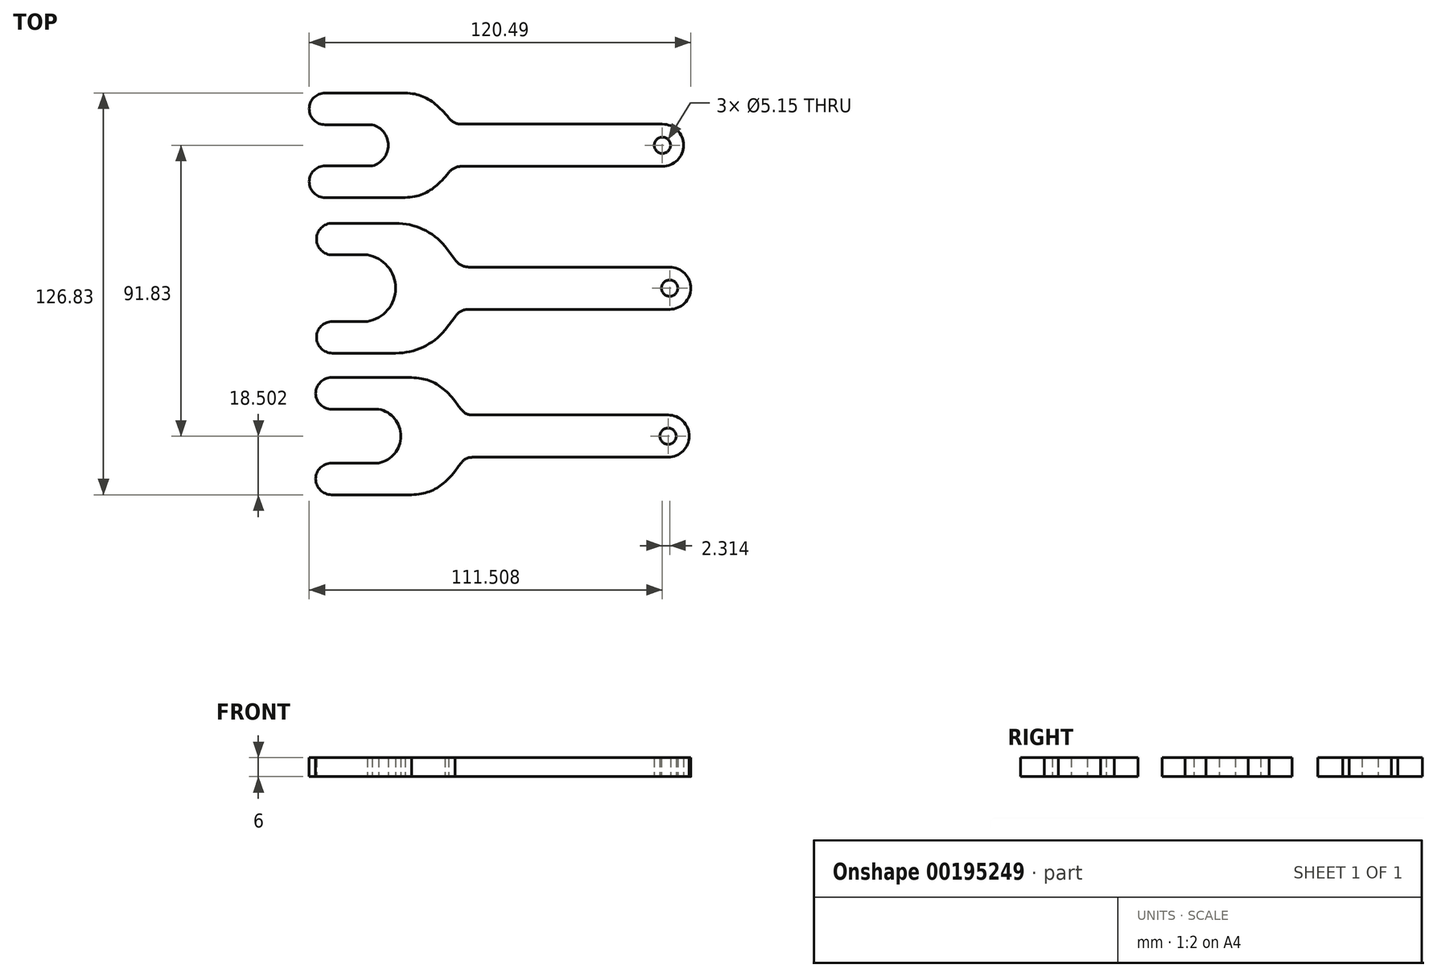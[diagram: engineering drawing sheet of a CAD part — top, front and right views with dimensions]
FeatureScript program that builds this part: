
annotation { "Feature Type Name" : "Feature", "Feature Type Description" : "" }
export const myFeature = defineFeature(function(context is Context, id is Id, definition is map)
    precondition{}
    {
        {
            var Q0;
            Q0=qCreatedBy(makeId("Top.planeOp"),FACE);
            var sketch = newSketch(context, id + "F0", { "sketchPlane" : qUnion([Q0])});
            skLineSegment(sketch, "E0.bottom", {"start": v(1.68, -10.5) * mm, "end": v(-4.7, -10.5) * mm});
            skLineSegment(sketch, "E0.top", {"start": v(1.68, 10.5) * mm, "end": v(-4.7, 10.5) * mm});
            skLineSegment(sketch, "E0.left", {"start": v(1.68, -10.5) * mm, "end": v(1.68, 10.5) * mm, "construction": true});
            skLineSegment(sketch, "E0.right", {"start": v(-4.7, -10.5) * mm, "end": v(-4.7, 10.5) * mm, "construction": true});
            skArc(sketch, "E1.trimOffspring", {"start": v(1.68, -10.5) * mm, "mid": v(10.63, 0) * mm, "end": v(1.68, 10.5) * mm});
            skPoint(sketch, "E2.oppositeSnap0", {"position": v(10.63, 0) * mm});
            skLineSegment(sketch, "E2.bottom", {"start": v(-9.33, -10.5) * mm, "end": v(1.68, -10.5) * mm});
            skLineSegment(sketch, "E2.top", {"start": v(-9.33, -20.5) * mm, "end": v(10.63, -20.5) * mm});
            skLineSegment(sketch, "E3.bottom", {"start": v(-4.7, 10.5) * mm, "end": v(-9.33, 10.5) * mm});
            skLineSegment(sketch, "E4.top", {"start": v(-4.7, 10.5) * mm, "end": v(1.68, 10.5) * mm});
            skLineSegment(sketch, "E5", {"start": v(10.63, 20.5) * mm, "end": v(-9.33, 20.5) * mm});
            skArc(sketch, "E6", {"start": v(10.63, -20.5) * mm, "mid": v(20.48, -17.98) * mm, "end": v(27.9, -11.05) * mm});
            skArc(sketch, "E7", {"start": v(-9.33, 20.5) * mm, "mid": v(-14.33, 15.5) * mm, "end": v(-9.33, 10.5) * mm});
            skArc(sketch, "E8", {"start": v(-9.33, -10.5) * mm, "mid": v(-14.33, -15.5) * mm, "end": v(-9.33, -20.5) * mm});
            skPoint(sketch, "E9.oppositeSnap0", {"position": v(31.13, 0) * mm});
            skLineSegment(sketch, "E10.top", {"start": v(33.66, 6.67) * mm, "end": v(97.17, 6.67) * mm});
            skLineSegment(sketch, "E11.MirrorCS", {"start": v(33.66, -6.67) * mm, "end": v(97.17, -6.67) * mm});
            skArc(sketch, "E12", {"start": v(97.17, 6.67) * mm, "mid": v(103.84, 0) * mm, "end": v(97.17, -6.67) * mm});
            skLineSegment(sketch, "E13", {"start": v(29.63, 8.7) * mm, "end": v(26.27, 13.25) * mm});
            skLineSegment(sketch, "E14", {"start": v(26.27, -13.25) * mm, "end": v(29.63, -8.7) * mm});
            skCircle(sketch, "E15", {"center": v(97.17, 0) * mm, "radius": 2.57 * mm});
            skPoint(sketch, "E16.MirrorCS.end.orphan", {"position": v(97.17, -6.67) * mm});
            skArc(sketch, "E17.trimOffspring", {"start": v(27.9, 11.05) * mm, "mid": v(20.48, 17.98) * mm, "end": v(10.63, 20.5) * mm});
            skPoint(sketch, "E18.MirrorCS.end.orphan", {"position": v(31.13, -6.67) * mm});
            skPoint(sketch, "E19.visualSharp", {"position": v(31.13, 6.67) * mm});
            skArc(sketch, "E19.filletArc", {"start": v(29.63, 8.7) * mm, "mid": v(31.4, 7.2) * mm, "end": v(33.66, 6.67) * mm});
            skArc(sketch, "E20.filletArc", {"start": v(33.66, -6.67) * mm, "mid": v(31.4, -7.2) * mm, "end": v(29.63, -8.7) * mm});
            skSolve(sketch);
        }
        {
            var Q0;
            {var subQ5=sQuery(id+"F0.wireOp",EDGE,"E1.trimOffspring");Q0=makeQuery(id+"F0.imprint","IMPRINT",FACE,{"disambiguationData":[TD([[makeQuery(id+"F0.imprint","IMPRINT",EDGE,{"derivedFrom":subQ5}),-1.0]])]});}
            extrude(context, id + "F1", {"entities" : qUnion([Q0]), "depth" : 6 * mm});
        }
        {
            var Q0;
            Q0=qCreatedBy(makeId("Top.planeOp"),FACE);
            var sketch = newSketch(context, id + "F2", { "sketchPlane" : qUnion([Q0])});
            skLineSegment(sketch, "E21.bottom", {"start": v(3.28, 38.62) * mm, "end": v(-3.08, 38.62) * mm});
            skLineSegment(sketch, "E21.top", {"start": v(3.28, 51.62) * mm, "end": v(-3.08, 51.62) * mm});
            skLineSegment(sketch, "E21.left", {"start": v(3.28, 38.62) * mm, "end": v(3.28, 51.62) * mm, "construction": true});
            skLineSegment(sketch, "E21.right", {"start": v(-3.08, 38.62) * mm, "end": v(-3.08, 51.62) * mm, "construction": true});
            skArc(sketch, "E22.trimOffspring", {"start": v(3.28, 38.62) * mm, "mid": v(8.32, 45.12) * mm, "end": v(3.28, 51.62) * mm});
            skPoint(sketch, "E23.oppositeSnap0", {"position": v(8.32, 45.12) * mm});
            skLineSegment(sketch, "E23.bottom", {"start": v(-11.65, 38.62) * mm, "end": v(3.28, 38.62) * mm});
            skLineSegment(sketch, "E24.bottom", {"start": v(-3.08, 51.62) * mm, "end": v(-11.65, 51.62) * mm});
            skLineSegment(sketch, "E25.top", {"start": v(-3.08, 51.62) * mm, "end": v(3.28, 51.62) * mm});
            skArc(sketch, "E26", {"start": v(-11.65, 61.62) * mm, "mid": v(-16.65, 56.62) * mm, "end": v(-11.65, 51.62) * mm});
            skPoint(sketch, "E27.oppositeSnap0", {"position": v(28.82, 45.12) * mm});
            skLineSegment(sketch, "E28.top", {"start": v(31.34, 51.8) * mm, "end": v(94.86, 51.8) * mm});
            skLineSegment(sketch, "E29.MirrorCS", {"start": v(31.34, 38.45) * mm, "end": v(94.86, 38.45) * mm});
            skArc(sketch, "E30", {"start": v(94.86, 51.8) * mm, "mid": v(101.53, 45.12) * mm, "end": v(94.86, 38.45) * mm});
            skCircle(sketch, "E31", {"center": v(94.86, 45.12) * mm, "radius": 2.57 * mm});
            skPoint(sketch, "E32.orphan", {"position": v(98.78, 49.12) * mm});
            skPoint(sketch, "E33.MirrorCS.end.orphan", {"position": v(98.78, 42.45) * mm});
            skPoint(sketch, "E34.MirrorCS.end.orphan", {"position": v(32.74, 42.45) * mm});
            skPoint(sketch, "E34.MirrorCS.start.orphan", {"position": v(32.74, 49.12) * mm});
            skPoint(sketch, "E35.visualSharp", {"position": v(28.82, 51.8) * mm});
            skArc(sketch, "E35.filletArc", {"start": v(27.32, 53.82) * mm, "mid": v(29.09, 52.33) * mm, "end": v(31.34, 51.8) * mm});
            skPoint(sketch, "E36.visualSharp", {"position": v(28.82, 38.45) * mm});
            skArc(sketch, "E36.filletArc", {"start": v(31.34, 38.45) * mm, "mid": v(29.09, 37.91) * mm, "end": v(27.32, 36.42) * mm});
            skLineSegment(sketch, "E37", {"start": v(-11.65, 61.62) * mm, "end": v(13.65, 61.62) * mm});
            skLineSegment(sketch, "E38", {"start": v(-11.65, 51.62) * mm, "end": v(-11.65, 61.62) * mm, "construction": true});
            skLineSegment(sketch, "E39", {"start": v(112.27, 45.12) * mm, "end": v(-30.7, 45.12) * mm, "construction": true});
            skLineSegment(sketch, "E40.MirrorCS", {"start": v(-11.65, 28.62) * mm, "end": v(13.65, 28.62) * mm});
            skArc(sketch, "E41.MirrorCS", {"start": v(-11.65, 28.62) * mm, "mid": v(-16.65, 33.62) * mm, "end": v(-11.65, 38.62) * mm});
            skFitSpline(sketch, "E42", {"points": [v(13.65, 61.62) * mm, v(27.32, 53.82) * mm], "startDerivative": vector(18.4, -0.56) * mm, "endDerivative": vector(11.88, -14.56) * mm});
            skFitSpline(sketch, "E43.MirrorCS", {"points": [v(13.65, 28.62) * mm, v(27.32, 36.42) * mm], "startDerivative": vector(18.4, 0.56) * mm, "endDerivative": vector(11.88, 14.56) * mm});
            skSolve(sketch);
        }
        {
            var Q0;
            {var subQ1=sQuery(id+"F2.wireOp",EDGE,"E22.trimOffspring");Q0=makeQuery(id+"F2.imprint","IMPRINT",FACE,{"disambiguationData":[TD([[makeQuery(id+"F2.imprint","IMPRINT",EDGE,{"derivedFrom":subQ1}),-1.0]])]});}
            extrude(context, id + "F3", {"entities" : qUnion([Q0]), "depth" : 6 * mm});
        }
        {
            var Q0;
            Q0=qCreatedBy(makeId("Top.planeOp"),FACE);
            var sketch = newSketch(context, id + "F4", { "sketchPlane" : qUnion([Q0])});
            skLineSegment(sketch, "E44.bottom", {"start": v(5.33, -55.2) * mm, "end": v(-1.04, -55.2) * mm});
            skLineSegment(sketch, "E44.top", {"start": v(5.33, -38.2) * mm, "end": v(-1.04, -38.2) * mm});
            skLineSegment(sketch, "E44.left", {"start": v(5.33, -55.2) * mm, "end": v(5.33, -38.2) * mm, "construction": true});
            skLineSegment(sketch, "E44.right", {"start": v(-1.04, -55.2) * mm, "end": v(-1.04, -38.2) * mm, "construction": true});
            skArc(sketch, "E45.trimOffspring", {"start": v(5.33, -55.2) * mm, "mid": v(12.32, -46.7) * mm, "end": v(5.33, -38.2) * mm});
            skPoint(sketch, "E46.oppositeSnap0", {"position": v(12.32, -46.7) * mm});
            skLineSegment(sketch, "E46.bottom", {"start": v(-9.6, -55.2) * mm, "end": v(5.33, -55.2) * mm});
            skLineSegment(sketch, "E47.bottom", {"start": v(-1.04, -38.2) * mm, "end": v(-9.6, -38.2) * mm});
            skLineSegment(sketch, "E48.top", {"start": v(-1.04, -38.2) * mm, "end": v(5.33, -38.2) * mm});
            skArc(sketch, "E49", {"start": v(-9.6, -28.2) * mm, "mid": v(-14.6, -33.2) * mm, "end": v(-9.6, -38.2) * mm});
            skPoint(sketch, "E50.oppositeSnap0", {"position": v(30.86, -45.24) * mm});
            skLineSegment(sketch, "E51.top", {"start": v(35.24, -40.04) * mm, "end": v(96.67, -40.04) * mm});
            skCircle(sketch, "E52", {"center": v(96.67, -46.7) * mm, "radius": 2.57 * mm});
            skPoint(sketch, "E53.MirrorCS.end.orphan", {"position": v(34.78, -47.91) * mm});
            skPoint(sketch, "E53.MirrorCS.start.orphan", {"position": v(34.78, -41.24) * mm});
            skPoint(sketch, "E54.visualSharp", {"position": v(30.86, -40.04) * mm});
            skLineSegment(sketch, "E55", {"start": v(-9.6, -28.2) * mm, "end": v(15.7, -28.2) * mm});
            skLineSegment(sketch, "E56", {"start": v(-9.6, -38.2) * mm, "end": v(-9.6, -28.2) * mm, "construction": true});
            skLineSegment(sketch, "E57", {"start": v(114.32, -46.7) * mm, "end": v(-28.65, -46.7) * mm, "construction": true});
            skLineSegment(sketch, "E58.MirrorCS", {"start": v(-9.6, -65.2) * mm, "end": v(15.7, -65.2) * mm});
            skArc(sketch, "E59.MirrorCS", {"start": v(-9.6, -65.2) * mm, "mid": v(-14.6, -60.2) * mm, "end": v(-9.6, -55.2) * mm});
            skFitSpline(sketch, "E60", {"points": [v(15.7, -28.2) * mm, v(29.37, -35.62) * mm], "startDerivative": vector(18.4, -0.56) * mm, "endDerivative": vector(11.88, -14.56) * mm});
            skFitSpline(sketch, "E61.MirrorCS", {"points": [v(15.7, -65.2) * mm, v(29.37, -57.8) * mm], "startDerivative": vector(18.4, 0.56) * mm, "endDerivative": vector(11.88, 14.56) * mm});
            skLineSegment(sketch, "E62.MirrorCS", {"start": v(35.24, -53.38) * mm, "end": v(96.67, -53.38) * mm});
            skArc(sketch, "E63", {"start": v(96.67, -40.04) * mm, "mid": v(103.34, -46.7) * mm, "end": v(96.67, -53.38) * mm});
            skFitSpline(sketch, "E64", {"points": [v(35.24, -40.04) * mm, v(29.37, -35.62) * mm], "startDerivative": vector(-8.02, 0) * mm, "endDerivative": vector(-7.66, 10.87) * mm});
            skFitSpline(sketch, "E65.MirrorCS", {"points": [v(35.24, -53.38) * mm, v(29.37, -57.8) * mm], "startDerivative": vector(-8.02, 0) * mm, "endDerivative": vector(-7.66, -10.87) * mm});
            skSolve(sketch);
        }
        {
            var Q0;
            {var subQ0=sQuery(id+"F4.wireOp",EDGE,"E45.trimOffspring");Q0=makeQuery(id+"F4.imprint","IMPRINT",FACE,{"disambiguationData":[TD([[makeQuery(id+"F4.imprint","IMPRINT",EDGE,{"derivedFrom":subQ0}),-1.0]])]});}
            extrude(context, id + "F5", {"entities" : qUnion([Q0]), "depth" : 6 * mm});
        }
    });
